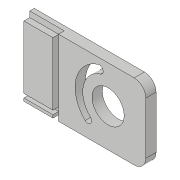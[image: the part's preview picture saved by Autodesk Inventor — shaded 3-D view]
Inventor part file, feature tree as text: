
AUTODESK INVENTOR PART (.ipt)
format: ipt  version: 2018.3 (Build 223284000, 284)  size: 227,840 bytes
history: native  units: in
note: dims shown in document units (in); Inventor stores cm internally (conversion verified against a paired STEP export)
features: extrude x2, fillet x1, sketch x1
ambient origin geometry x8: Origin, YZ Plane, XZ Plane, XY Plane, X Axis, Y Axis, Z Axis, Center Point
bodies: Solid1 (feature_tree)
feature tree (4):
  extrude  "Extrusion1"  Depth=2.625in
  extrude  "Extrusion3"  Depth=0.082in
  fillet  "Fillet1"  Radius=0.8125in
  sketch  "Sketch1"  dims[d0=1.625in d1=2.625in d8=0.6925in d9=0.8125in d12=0.221in d13=0.0in d25=0.8125in d26=0.625in d27=0.119in d28=0.125in d29=0.125in d30=0.0in d31=0.25in d32=1.0in d33=1.25in d38=0.0625in d39=0.085in d49=0.082in d50=0.628in]
